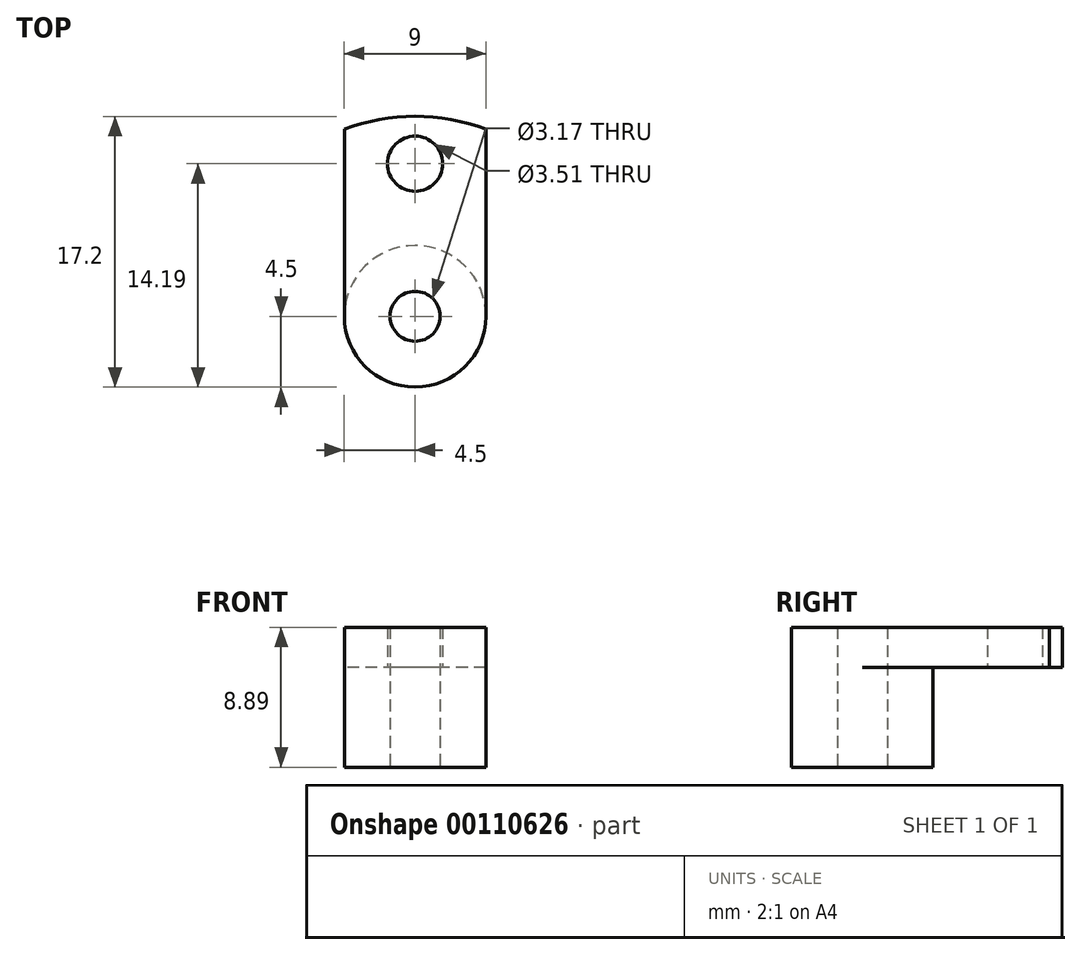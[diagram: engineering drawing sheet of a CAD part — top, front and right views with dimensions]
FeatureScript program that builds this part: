
annotation { "Feature Type Name" : "Feature", "Feature Type Description" : "" }
export const myFeature = defineFeature(function(context is Context, id is Id, definition is map)
    precondition{}
    {
        {
            var Q0;
            Q0=qCreatedBy(makeId("Top.planeOp"),FACE);
            var sketch = newSketch(context, id + "F0", { "sketchPlane" : qUnion([Q0])});
            skCircle(sketch, "E0", {"center": v(0, 0) * mm, "radius": 4.5 * mm});
            skCircle(sketch, "E1", {"center": v(0, 0) * mm, "radius": 1.59 * mm});
            skSolve(sketch);
        }
        {
            var Q0;
            Q0 = qSketchRegion(id + "F0", true);
            extrude(context, id + "F1", {"entities" : qUnion([Q0]), "depth" : 6.35 * mm});
        }
        {
            var Q0;
            Q0=makeQuery(id+"F1.opExtrude","CAP_FACE",FACE,{"disambiguationData":[OSD([sQuery(id+"F0.wireOp",EDGE,"E0"),sQuery(id+"F0.wireOp",EDGE,"E1")])],"isStart":false});
            var sketch = newSketch(context, id + "F2", { "sketchPlane" : qUnion([Q0])});
            skCircle(sketch, "E2", {"center": v(0, 0) * mm, "radius": 12.7 * mm});
            skCircle(sketch, "E3", {"center": v(0, 0) * mm, "radius": 1.59 * mm});
            skCircle(sketch, "E4", {"center": v(0, 9.7) * mm, "radius": 1.75 * mm});
            skCircle(sketch, "E5.1.0", {"center": v(-8.4, 4.85) * mm, "radius": 1.75 * mm});
            skCircle(sketch, "E5.2.0", {"center": v(-8.4, -4.85) * mm, "radius": 1.75 * mm});
            skCircle(sketch, "E5.3.0", {"center": v(0, -9.7) * mm, "radius": 1.75 * mm});
            skCircle(sketch, "E5.4.0", {"center": v(8.4, -4.85) * mm, "radius": 1.75 * mm});
            skCircle(sketch, "E5.5.0", {"center": v(8.4, 4.85) * mm, "radius": 1.75 * mm});
            skCircle(sketch, "E6", {"center": v(0, 0) * mm, "radius": 9.7 * mm, "construction": true});
            skSolve(sketch);
        }
        {
            var Q0;
            Q0 = qSketchRegion(id + "F2", true);
            extrude(context, id + "F3", {"entities" : qUnion([Q0]), "operationType" : NewBodyOperationType.ADD, "depth" : 2.54 * mm});
        }
        {
            var Q0;
            Q0=makeQuery(id+"F3.opExtrude","CAP_FACE",FACE,{"disambiguationData":[OSD([sQuery(id+"F2.wireOp",EDGE,"E2"),sQuery(id+"F2.wireOp",EDGE,"E3"),sQuery(id+"F2.wireOp",EDGE,"E4"),sQuery(id+"F2.wireOp",EDGE,"E5.1.0"),sQuery(id+"F2.wireOp",EDGE,"E5.2.0"),sQuery(id+"F2.wireOp",EDGE,"E5.3.0"),sQuery(id+"F2.wireOp",EDGE,"E5.4.0"),sQuery(id+"F2.wireOp",EDGE,"E5.5.0")])],"isStart":false});
            var sketch = newSketch(context, id + "F4", { "sketchPlane" : qUnion([Q0])});
            skArc(sketch, "E7", {"start": v(-4.5, 0) * mm, "mid": v(0, -4.5) * mm, "end": v(4.5, 0) * mm});
            skLineSegment(sketch, "E8.bottom", {"start": v(29.3, 24.1) * mm, "end": v(-29.3, 24.1) * mm});
            skLineSegment(sketch, "E8.top", {"start": v(29.3, -24.1) * mm, "end": v(-29.3, -24.1) * mm});
            skLineSegment(sketch, "E8.left", {"start": v(29.3, 24.1) * mm, "end": v(29.3, -24.1) * mm});
            skLineSegment(sketch, "E8.right", {"start": v(-29.3, 24.1) * mm, "end": v(-29.3, -24.1) * mm});
            skLineSegment(sketch, "E9", {"start": v(-4.5, 0) * mm, "end": v(-4.5, 11.88) * mm});
            skLineSegment(sketch, "E10", {"start": v(4.5, 0) * mm, "end": v(4.5, 11.88) * mm});
            skArc(sketch, "E11", {"start": v(4.5, 11.88) * mm, "mid": v(0, 12.7) * mm, "end": v(-4.5, 11.88) * mm});
            skSolve(sketch);
        }
        {
            var Q0;
            Q0 = qSketchRegion(id + "F4", true);
            extrude(context, id + "F5", {"entities" : qUnion([Q0]), "operationType" : NewBodyOperationType.REMOVE, "oppositeDirection" : true, "depth" : 25.4 * mm});
        }
    });
